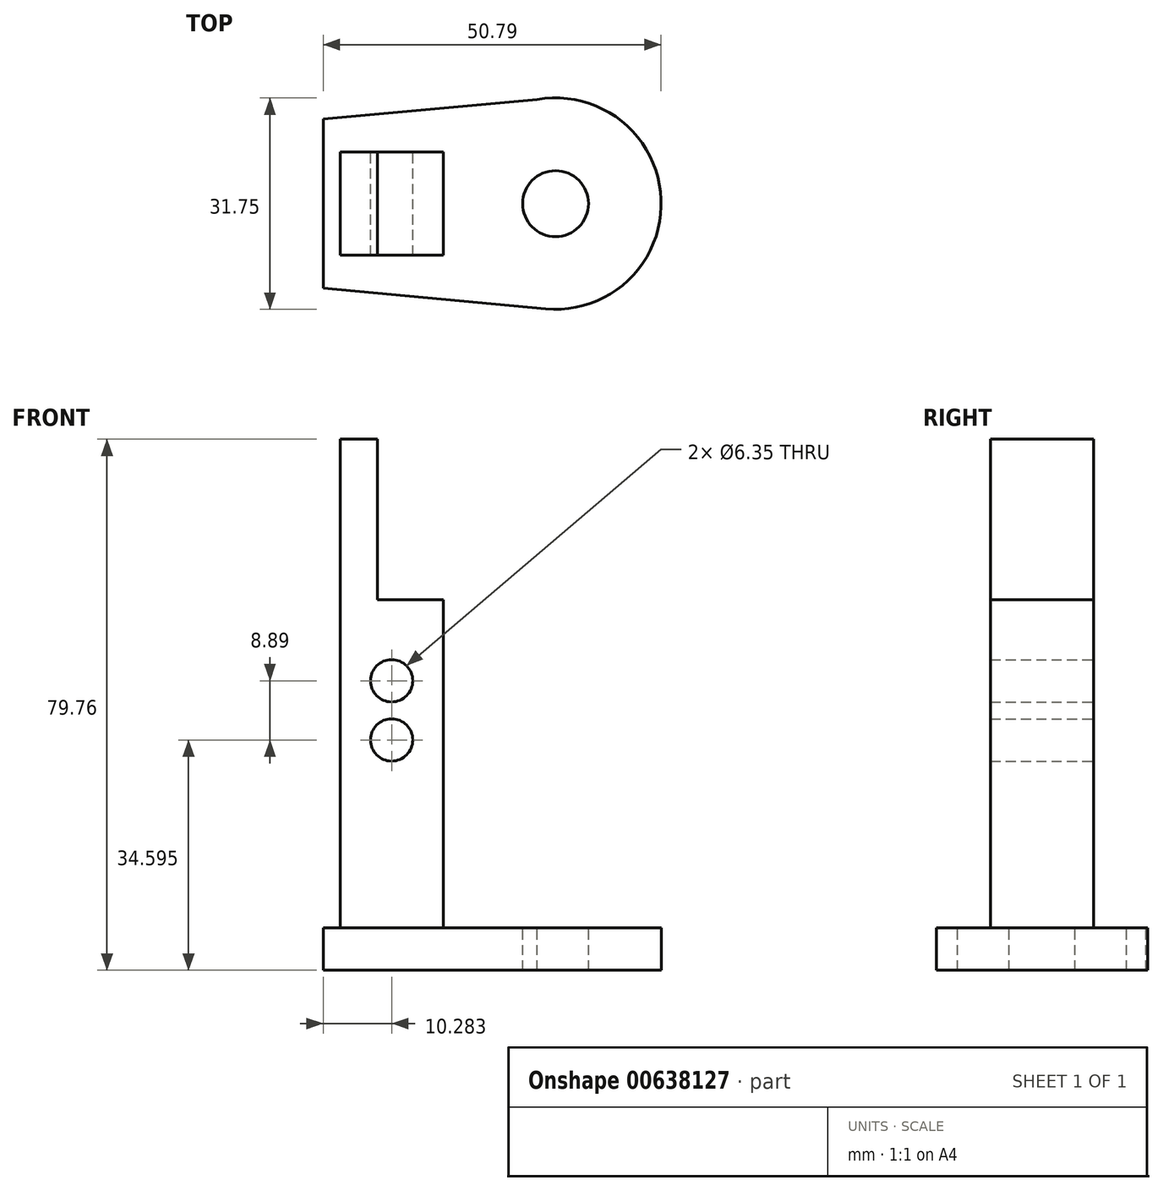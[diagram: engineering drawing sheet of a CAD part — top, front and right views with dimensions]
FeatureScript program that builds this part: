
annotation { "Feature Type Name" : "Feature", "Feature Type Description" : "" }
export const myFeature = defineFeature(function(context is Context, id is Id, definition is map)
    precondition{}
    {
        {
            var Q0;
            Q0=qCreatedBy(makeId("Top.planeOp"),FACE);
            var sketch = newSketch(context, id + "F0", { "sketchPlane" : qUnion([Q0])});
            skCircle(sketch, "E0", {"center": v(0, 0) * mm, "radius": 4.95 * mm});
            skLineSegment(sketch, "E1", {"start": v(0, 0) * mm, "end": v(-34.93, 0) * mm, "construction": true});
            skLineSegment(sketch, "E2", {"start": v(-34.93, 12.7) * mm, "end": v(-34.93, -12.7) * mm});
            skLineSegment(sketch, "E3", {"start": v(-34.93, 12.7) * mm, "end": v(-2.76, 15.63) * mm});
            skLineSegment(sketch, "E4", {"start": v(-34.93, -12.7) * mm, "end": v(-1.47, -15.8) * mm});
            skArc(sketch, "E5", {"start": v(-2.76, 15.63) * mm, "mid": v(-15.86, -0.65) * mm, "end": v(-1.47, -15.8) * mm, "construction": true});
            skArc(sketch, "E6", {"start": v(-1.47, -15.8) * mm, "mid": v(15.86, 0.65) * mm, "end": v(-2.76, 15.63) * mm});
            skSolve(sketch);
        }
        {
            var Q0;
            Q0 = qSketchRegion(id + "F0", true);
            extrude(context, id + "F1", {"entities" : qUnion([Q0]), "oppositeDirection" : true, "depth" : 6.35 * mm, "offsetDistance" : 25.4 * mm});
        }
        {
            var Q0;
            Q0=qCreatedBy(makeId("Front.planeOp"),FACE);
            var sketch = newSketch(context, id + "F2", { "sketchPlane" : qUnion([Q0])});
            skLineSegment(sketch, "E7", {"start": v(-32.38, 0) * mm, "end": v(-32.38, 73.4) * mm});
            skLineSegment(sketch, "E8", {"start": v(-32.38, 73.4) * mm, "end": v(-26.8, 73.4) * mm});
            skLineSegment(sketch, "E9", {"start": v(-26.8, 73.4) * mm, "end": v(-26.8, 49.28) * mm});
            skLineSegment(sketch, "E10", {"start": v(-26.8, 49.28) * mm, "end": v(-16.9, 49.28) * mm});
            skLineSegment(sketch, "E11", {"start": v(-16.9, 49.28) * mm, "end": v(-16.9, 0) * mm});
            skLineSegment(sketch, "E12", {"start": v(-16.9, 0) * mm, "end": v(-32.38, 0) * mm});
            skLineSegment(sketch, "E13", {"start": v(-16.9, 37.13) * mm, "end": v(-24.64, 37.13) * mm, "construction": true});
            skLineSegment(sketch, "E14", {"start": v(-24.64, 37.13) * mm, "end": v(-32.38, 37.13) * mm, "construction": true});
            skCircle(sketch, "E15", {"center": v(-24.64, 37.13) * mm, "radius": 3.18 * mm});
            skCircle(sketch, "E16", {"center": v(-24.64, 28.24) * mm, "radius": 3.18 * mm});
            skSolve(sketch);
        }
        {
            var Q0;
            Q0 = qSketchRegion(id + "F2", true);
            extrude(context, id + "F3", {"entities" : qUnion([Q0]), "operationType" : NewBodyOperationType.ADD, "depth" : 7.75 * mm, "offsetDistance" : 25.4 * mm, "hasSecondDirection" : true, "secondDirectionOppositeDirection" : true, "secondDirectionDepth" : 7.75 * mm});
        }
    });
